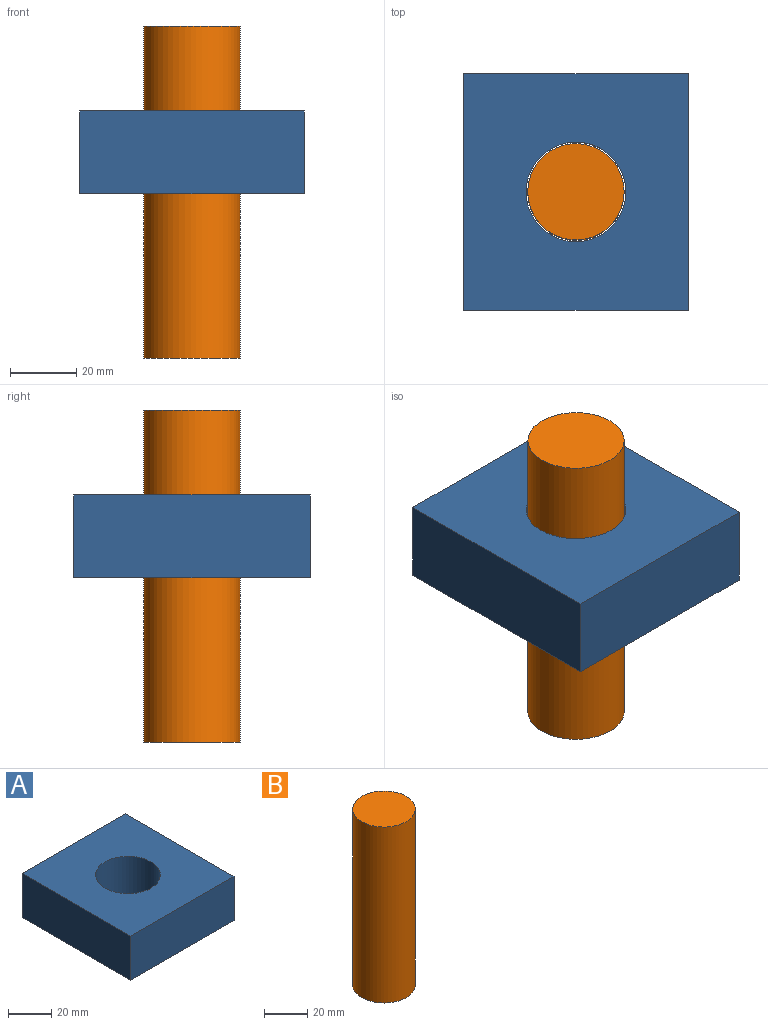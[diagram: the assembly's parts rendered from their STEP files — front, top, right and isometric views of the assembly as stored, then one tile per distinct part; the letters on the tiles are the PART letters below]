
ASSEMBLY  parts=2 mates=1
PART A: 7 faces, bbox 67.7x71.3x25 mm
  f0: plane 67.69x25mm, normal (0,-1,0), area 1692.2mm2, adj f1,f4,f5,f6
  f1: plane 71.29x25mm, normal (1,0,0), area 1782.2mm2, adj f0,f2,f5,f6
  f2: plane 67.69x25mm, normal (0,1,0), area 1692.2mm2, adj f1,f4,f5,f6
  f3: cylinder r=15mm len=30mm, axis (0,0,-1), area 2356.2mm2, adj f5,f6
  f4: plane 71.29x25mm, normal (-1,0,0), area 1782.2mm2, adj f0,f2,f5,f6
  f5: plane 71.29x67.69mm, normal (0,0,1), area 4118.4mm2, adj f0,f1,f2,f3,f4
  f6: plane 71.29x67.69mm, normal (0,0,-1), area 4118.4mm2, adj f0,f1,f2,f3,f4
PART B: 3 faces, bbox 29x29x100 mm
  f0: cylinder r=14.5mm len=100mm, axis (0,0,-1), area 9110.6mm2, adj f1,f2
  f1: plane 29x29mm, normal (0,0,1), area 660.5mm2, adj f0
  f2: plane 29x29mm, normal (0,0,-1), area 660.5mm2, adj f0
PLACE A t=(2.6,-11.5,-3.5)mm
PLACE B t=(2.6,-11.5,-52.9)mm
MATE slider B.f0 <-> A.f3  axis (0,0,1) through (2.6,-11.5,47.1)mm
